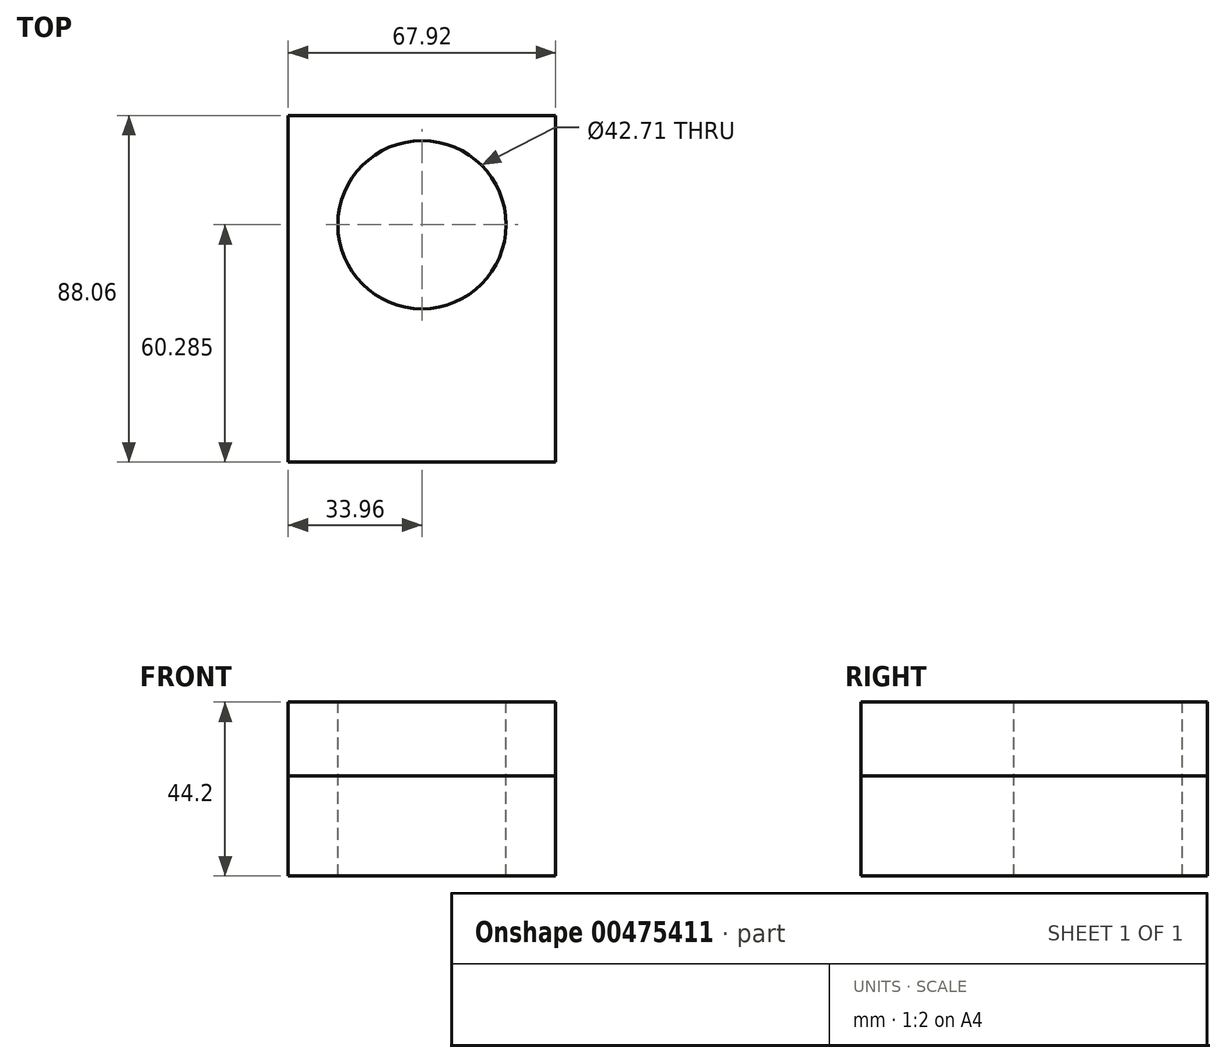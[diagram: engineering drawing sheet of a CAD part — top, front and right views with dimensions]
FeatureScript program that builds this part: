
annotation { "Feature Type Name" : "Feature", "Feature Type Description" : "" }
export const myFeature = defineFeature(function(context is Context, id is Id, definition is map)
    precondition{}
    {
        {
            var Q0;
            Q0=qCreatedBy(makeId("Top.planeOp"),FACE);
            var sketch = newSketch(context, id + "F0", { "sketchPlane" : qUnion([Q0])});
            skLineSegment(sketch, "E0.bottom", {"start": v(33.96, 44.03) * mm, "end": v(-33.96, 44.03) * mm});
            skLineSegment(sketch, "E0.top", {"start": v(33.96, -44.03) * mm, "end": v(-33.96, -44.03) * mm});
            skLineSegment(sketch, "E0.left", {"start": v(33.96, 44.03) * mm, "end": v(33.96, -44.03) * mm});
            skLineSegment(sketch, "E0.right", {"start": v(-33.96, 44.03) * mm, "end": v(-33.96, -44.03) * mm});
            skPoint(sketch, "E0.middle", {"position": v(0, 0) * mm});
            skSolve(sketch);
        }
        {
            var Q0;
            Q0=makeQuery(id+"F0.imprint","IMPRINT",FACE,{"disambiguationData":[TD([[makeQuery(id+"F0.imprint","IMPRINT",EDGE,{"derivedFrom":sQuery(id+"F0.wireOp",EDGE,"E0.bottom")}),1.0]])]});
            extrude(context, id + "F1", {"entities" : qUnion([Q0]), "depth" : 44.2 * mm});
        }
        {
            var Q0;
            Q0=makeQuery(id+"F1.opExtrude","CAP_FACE",FACE,{"disambiguationData":[OSD([sQuery(id+"F0.wireOp",EDGE,"E0.bottom"),sQuery(id+"F0.wireOp",EDGE,"E0.top"),sQuery(id+"F0.wireOp",EDGE,"E0.left"),sQuery(id+"F0.wireOp",EDGE,"E0.right")])],"isStart":false});
            var sketch = newSketch(context, id + "F2", { "sketchPlane" : qUnion([Q0])});
            skCircle(sketch, "E1", {"center": v(0, 16.26) * mm, "radius": 21.36 * mm});
            skSolve(sketch);
        }
        {
            var Q0;
            Q0=makeQuery(id+"F2.imprint","IMPRINT",FACE,{"disambiguationData":[TD([[makeQuery(id+"F2.imprint","IMPRINT",EDGE,{"derivedFrom":sQuery(id+"F2.wireOp",EDGE,"E1")}),1.0]])]});
            extrude(context, id + "F3", {"entities" : qUnion([Q0]), "operationType" : NewBodyOperationType.REMOVE, "endBound" : BoundingType.THROUGH_ALL, "oppositeDirection" : true, "depth" : 25.4 * mm});
        }
        {
            var Q0;
            Q0=makeQuery(id+"F0.imprint","IMPRINT",FACE,{"disambiguationData":[TD([[makeQuery(id+"F0.imprint","IMPRINT",EDGE,{"derivedFrom":sQuery(id+"F0.wireOp",EDGE,"E0.bottom")}),1.0]])]});
            extrude(context, id + "F4", {"entities" : qUnion([Q0]), "depth" : 25.4 * mm});
        }
    });
